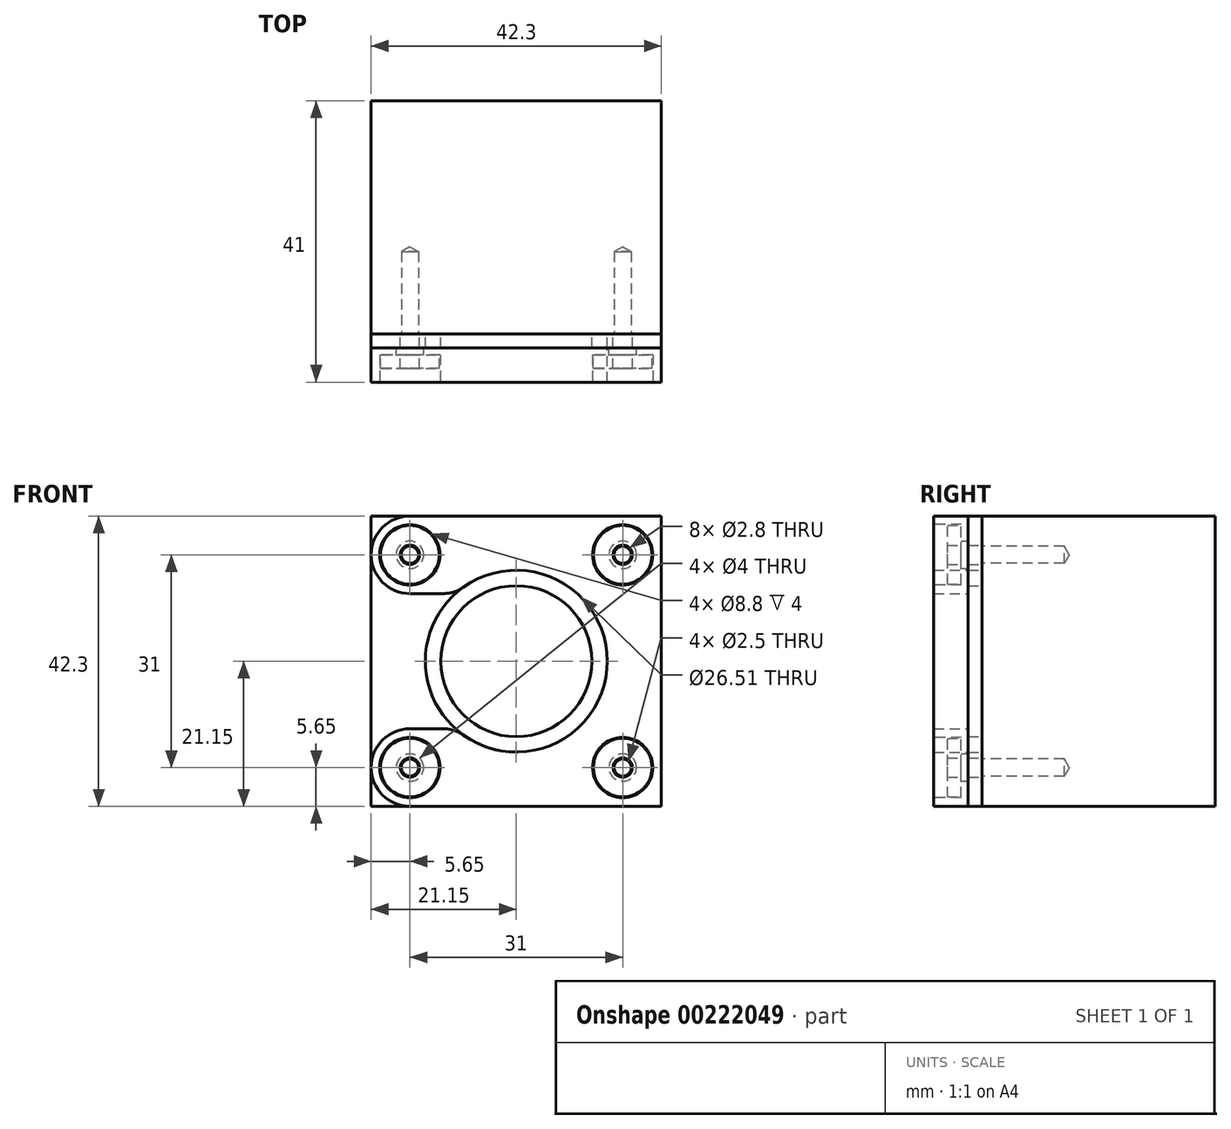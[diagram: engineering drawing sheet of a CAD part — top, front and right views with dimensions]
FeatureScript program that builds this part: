
annotation { "Feature Type Name" : "Feature", "Feature Type Description" : "" }
export const myFeature = defineFeature(function(context is Context, id is Id, definition is map)
    precondition{}
    {
        {
            var Q0;
            Q0=qCreatedBy(makeId("Front.planeOp"),FACE);
            var sketch = newSketch(context, id + "F0", { "sketchPlane" : qUnion([Q0])});
            skLineSegment(sketch, "E0.bottom", {"start": v(21.15, -21.15) * mm, "end": v(-21.15, -21.15) * mm});
            skLineSegment(sketch, "E0.top", {"start": v(21.15, 21.15) * mm, "end": v(-21.15, 21.15) * mm});
            skLineSegment(sketch, "E0.left", {"start": v(21.15, -21.15) * mm, "end": v(21.15, 21.15) * mm});
            skLineSegment(sketch, "E0.right", {"start": v(-21.15, -21.15) * mm, "end": v(-21.15, 21.15) * mm});
            skPoint(sketch, "E0.middle", {"position": v(0, 0) * mm});
            skSolve(sketch);
        }
        {
            var Q0;
            Q0=makeQuery(id+"F0.imprint","IMPRINT",FACE,{"disambiguationData":[TD([[makeQuery(id+"F0.imprint","IMPRINT",EDGE,{"derivedFrom":sQuery(id+"F0.wireOp",EDGE,"E0.bottom")}),-1.0]])]});
            extrude(context, id + "F1", {"entities" : qUnion([Q0]), "depth" : 34 * mm, "offsetDistance" : 25 * mm});
        }
        {
            var Q0;
            Q0=makeQuery(id+"F1.opExtrude","CAP_FACE",FACE,{"disambiguationData":[OSD([sQuery(id+"F0.wireOp",EDGE,"E0.bottom"),sQuery(id+"F0.wireOp",EDGE,"E0.top"),sQuery(id+"F0.wireOp",EDGE,"E0.left"),sQuery(id+"F0.wireOp",EDGE,"E0.right")])],"isStart":false});
            var sketch = newSketch(context, id + "F2", { "sketchPlane" : qUnion([Q0])});
            skCircle(sketch, "E1", {"center": v(0, 0) * mm, "radius": 11 * mm});
            skSolve(sketch);
        }
        {
            var Q0;
            Q0=makeQuery(id+"F2.imprint","IMPRINT",FACE,{"disambiguationData":[TD([[makeQuery(id+"F2.imprint","IMPRINT",EDGE,{"derivedFrom":sQuery(id+"F2.wireOp",EDGE,"E1")}),1.0]])]});
            extrude(context, id + "F3", {"entities" : qUnion([Q0]), "operationType" : NewBodyOperationType.ADD, "depth" : 2 * mm, "offsetDistance" : 25 * mm});
        }
        {
            var Q0;
            Q0=makeQuery(id+"F1.opExtrude","CAP_FACE",FACE,{"disambiguationData":[OSD([sQuery(id+"F0.wireOp",EDGE,"E0.bottom"),sQuery(id+"F0.wireOp",EDGE,"E0.top"),sQuery(id+"F0.wireOp",EDGE,"E0.left"),sQuery(id+"F0.wireOp",EDGE,"E0.right")])],"isStart":false});
            var sketch = newSketch(context, id + "F4", { "sketchPlane" : qUnion([Q0])});
            skLineSegment(sketch, "E2.bottom", {"start": v(15.5, 15.5) * mm, "end": v(-15.5, 15.5) * mm});
            skLineSegment(sketch, "E2.top", {"start": v(15.5, -15.5) * mm, "end": v(-15.5, -15.5) * mm});
            skLineSegment(sketch, "E2.left", {"start": v(15.5, 15.5) * mm, "end": v(15.5, -15.5) * mm});
            skLineSegment(sketch, "E2.right", {"start": v(-15.5, 15.5) * mm, "end": v(-15.5, -15.5) * mm});
            skPoint(sketch, "E2.middle", {"position": v(0, 0) * mm});
            skSolve(sketch);
        }
        {
            var Q0;
            Q0=sQuery(id+"F4.wireOp",VERTEX,"E2.right.start");
            var Q1;
            Q1=sQuery(id+"F4.wireOp",VERTEX,"E2.left.start");
            var Q2;
            Q2=sQuery(id+"F4.wireOp",VERTEX,"E2.left.end");
            var Q3;
            Q3=sQuery(id+"F4.wireOp",VERTEX,"E2.top.end");
            var Q4;
            Q4=makeQuery(id+"F1.opExtrude","SWEPT_BODY",BODY,{"disambiguationData":[OSD([sQuery(id+"F0.wireOp",EDGE,"E0.bottom"),sQuery(id+"F0.wireOp",EDGE,"E0.top"),sQuery(id+"F0.wireOp",EDGE,"E0.left"),sQuery(id+"F0.wireOp",EDGE,"E0.right")])]});
            hole(context, id + "F5", {"style" : HoleStyle.SIMPLE, "endStyle" : HoleEndStyle.BLIND, "holeDiameter" : 2.5 * mm, "majorDiameter" : 5 * mm, "holeDepth" : 12 * mm, "isTappedThrough" : true, "tappedDepth" : 12 * mm, "tapClearance" : 3, "locations" : qUnion([Q0, Q1, Q2, Q3]), "scope" : qUnion([Q4])});
        }
        {
            var Q0;
            Q0=makeQuery(id+"F1.opExtrude","CAP_FACE",FACE,{"disambiguationData":[OSD([sQuery(id+"F0.wireOp",EDGE,"E0.bottom"),sQuery(id+"F0.wireOp",EDGE,"E0.top"),sQuery(id+"F0.wireOp",EDGE,"E0.left"),sQuery(id+"F0.wireOp",EDGE,"E0.right")])],"isStart":false});
            var sketch = newSketch(context, id + "F6", { "sketchPlane" : qUnion([Q0])});
            skCircle(sketch, "E3.0", {"center": v(0, 0) * mm, "radius": 13.25 * mm});
            skCircle(sketch, "E4.0", {"center": v(15.5, 15.5) * mm, "radius": 1.25 * mm});
            skCircle(sketch, "E4.1", {"center": v(15.5, -15.5) * mm, "radius": 1.25 * mm});
            skCircle(sketch, "E4.2", {"center": v(-15.5, -15.5) * mm, "radius": 1.25 * mm});
            skCircle(sketch, "E4.3", {"center": v(-15.5, 15.5) * mm, "radius": 1.25 * mm});
            skCircle(sketch, "E5", {"center": v(15.5, 15.5) * mm, "radius": 1.4 * mm});
            skCircle(sketch, "E6", {"center": v(-15.5, 15.5) * mm, "radius": 1.4 * mm});
            skCircle(sketch, "E7", {"center": v(15.5, -15.5) * mm, "radius": 1.4 * mm});
            skCircle(sketch, "E8", {"center": v(-15.5, -15.5) * mm, "radius": 1.4 * mm});
            skSolve(sketch);
        }
        {
            var Q0;
            Q0=makeQuery(id+"F6.imprint","IMPRINT",FACE,{"disambiguationData":[TD([[makeQuery(id+"F6.imprint","IMPRINT",EDGE,{"derivedFrom":sQuery(id+"F6.wireOp",EDGE,"E3.0")}),-1.0]])]});
            extrude(context, id + "F7", {"entities" : qUnion([Q0]), "depth" : 2 * mm, "offsetDistance" : 25 * mm});
        }
        {
            var Q0;
            Q0=makeQuery(id+"F7.opExtrude","CAP_FACE",FACE,{"disambiguationData":[OSD([sQuery(id+"F0.wireOp",EDGE,"E0.bottom"),sQuery(id+"F0.wireOp",EDGE,"E0.top"),sQuery(id+"F0.wireOp",EDGE,"E0.left"),sQuery(id+"F0.wireOp",EDGE,"E0.right"),sQuery(id+"F6.wireOp",EDGE,"E3.0"),sQuery(id+"F6.wireOp",EDGE,"E5"),sQuery(id+"F6.wireOp",EDGE,"E6"),sQuery(id+"F6.wireOp",EDGE,"E7"),sQuery(id+"F6.wireOp",EDGE,"E8")])],"isStart":false});
            var sketch = newSketch(context, id + "F8", { "sketchPlane" : qUnion([Q0])});
            skCircle(sketch, "E9.0", {"center": v(-15.5, 15.5) * mm, "radius": 1.4 * mm});
            skCircle(sketch, "E10", {"center": v(-15.5, 15.5) * mm, "radius": 5.65 * mm});
            skCircle(sketch, "E11", {"center": v(15.5, 15.5) * mm, "radius": 5.65 * mm});
            skCircle(sketch, "E12", {"center": v(15.5, -15.5) * mm, "radius": 5.65 * mm});
            skCircle(sketch, "E13", {"center": v(-15.5, -15.5) * mm, "radius": 5.65 * mm});
            skLineSegment(sketch, "E14.0", {"start": v(15.5, 21.15) * mm, "end": v(-15.5, 21.15) * mm});
            skLineSegment(sketch, "E15.0", {"start": v(21.15, -15.5) * mm, "end": v(21.15, 15.5) * mm});
            skLineSegment(sketch, "E16.0", {"start": v(15.5, -21.15) * mm, "end": v(-15.5, -21.15) * mm});
            skLineSegment(sketch, "E17", {"start": v(-15.5, 9.85) * mm, "end": v(-8.87, 9.85) * mm});
            skLineSegment(sketch, "E18", {"start": v(-15.5, -9.85) * mm, "end": v(-8.87, -9.85) * mm});
            skPoint(sketch, "E19.orphan", {"position": v(21.15, 21.15) * mm});
            skPoint(sketch, "E20.orphan", {"position": v(-21.15, 21.15) * mm});
            skPoint(sketch, "E21.orphan", {"position": v(21.15, -21.15) * mm});
            skPoint(sketch, "E22.orphan", {"position": v(-21.15, -21.15) * mm});
            skCircle(sketch, "E23", {"center": v(15.5, 15.5) * mm, "radius": 2 * mm});
            skCircle(sketch, "E24", {"center": v(-15.5, 15.5) * mm, "radius": 2 * mm});
            skCircle(sketch, "E25", {"center": v(15.5, -15.5) * mm, "radius": 2 * mm});
            skCircle(sketch, "E26", {"center": v(-15.5, -15.5) * mm, "radius": 2 * mm});
            skSolve(sketch);
        }
        {
            var Q0;
            Q0=makeQuery(id+"F8.imprint","IMPRINT",FACE,{"disambiguationData":[TD([[makeQuery(id+"F8.imprint","IMPRINT",EDGE,{"derivedFrom":sQuery(id+"F8.wireOp",EDGE,"E23")}),-1.0]])]});
            var Q1;
            {var subQ1=makeQuery(id+"F7.opExtrude","CAP_EDGE",EDGE,{"disambiguationData":[OSD([sQuery(id+"F0.wireOp",EDGE,"E0.top")])],"isStart":false});var subQ3=makeQuery(id+"F7.opExtrude","CAP_EDGE",EDGE,{"disambiguationData":[OSD([sQuery(id+"F0.wireOp",EDGE,"E0.left")])],"isStart":false});var subQ5=makeQuery(id+"F8.imprint","INTERSECT",VERTEX,{"derivedFrom":[subQ1,subQ3]});Q1=makeQuery(id+"F8.imprint","IMPRINT",FACE,{"disambiguationData":[TD([[makeQuery(id+"F8.imprint","IMPRINT",EDGE,{"disambiguationData":[TD([[subQ5,-1.0]])],"derivedFrom":subQ1}),1.0]])]});}
            var Q2;
            {var subQ9=sQuery(id+"F8.wireOp",EDGE,"E14.0");Q2=makeQuery(id+"F8.imprint","IMPRINT",FACE,{"disambiguationData":[TD([[makeQuery(id+"F8.imprint","IMPRINT",EDGE,{"derivedFrom":subQ9}),1.0]])]});}
            var Q3;
            Q3=makeQuery(id+"F8.imprint","IMPRINT",FACE,{"disambiguationData":[TD([[makeQuery(id+"F8.imprint","IMPRINT",EDGE,{"derivedFrom":sQuery(id+"F8.wireOp",EDGE,"E25")}),-1.0]])]});
            var Q4;
            {var subQ1=makeQuery(id+"F7.opExtrude","CAP_EDGE",EDGE,{"disambiguationData":[OSD([sQuery(id+"F0.wireOp",EDGE,"E0.left")])],"isStart":false});var subQ3=makeQuery(id+"F7.opExtrude","CAP_EDGE",EDGE,{"disambiguationData":[OSD([sQuery(id+"F0.wireOp",EDGE,"E0.bottom")])],"isStart":false});var subQ5=makeQuery(id+"F8.imprint","INTERSECT",VERTEX,{"derivedFrom":[subQ3,subQ1]});Q4=makeQuery(id+"F8.imprint","IMPRINT",FACE,{"disambiguationData":[TD([[makeQuery(id+"F8.imprint","IMPRINT",EDGE,{"disambiguationData":[TD([[subQ5,-1.0]])],"derivedFrom":subQ3}),-1.0]])]});}
            var Q5;
            Q5=makeQuery(id+"F8.imprint","IMPRINT",FACE,{"disambiguationData":[TD([[makeQuery(id+"F8.imprint","IMPRINT",EDGE,{"derivedFrom":sQuery(id+"F8.wireOp",EDGE,"E24")}),-1.0]])]});
            var Q6;
            Q6=makeQuery(id+"F8.imprint","IMPRINT",FACE,{"disambiguationData":[TD([[makeQuery(id+"F8.imprint","IMPRINT",EDGE,{"derivedFrom":sQuery(id+"F8.wireOp",EDGE,"E26")}),-1.0]])]});
            var Q7;
            Q7=sQuery(id+"F8.wireOp",EDGE,"E17");
            var Q8;
            Q8=sQuery(id+"F8.wireOp",EDGE,"E18");
            extrude(context, id + "F9", {"entities" : qUnion([Q0, Q1, Q2, Q3, Q4, Q5, Q6]), "surfaceEntities" : qUnion([Q7, Q8]), "depth" : 5 * mm, "offsetDistance" : 25 * mm});
        }
        {
            var Q0;
            Q0=makeQuery(id+"F9.opExtrude","SWEPT_EDGE",EDGE,{"disambiguationData":[OSD([sQuery(id+"F6.wireOp",EDGE,"E3.0"),sQuery(id+"F8.wireOp",EDGE,"E18")])]});
            var Q1;
            Q1=makeQuery(id+"F9.opExtrude","SWEPT_EDGE",EDGE,{"disambiguationData":[OSD([sQuery(id+"F6.wireOp",EDGE,"E3.0"),sQuery(id+"F8.wireOp",EDGE,"E17")])]});
            fillet(context, id + "F10", {"entities" : qUnion([Q0, Q1]), "radius" : 5 * mm, "tangentPropagation" : true, "allowEdgeOverflow" : false});
        }
        {
            var Q0;
            Q0=makeQuery(id+"F9.opExtrude","CAP_FACE",FACE,{"disambiguationData":[OSD([sQuery(id+"F0.wireOp",EDGE,"E0.bottom"),sQuery(id+"F0.wireOp",EDGE,"E0.top"),sQuery(id+"F0.wireOp",EDGE,"E0.left"),sQuery(id+"F0.wireOp",EDGE,"E0.right"),sQuery(id+"F6.wireOp",EDGE,"E3.0"),sQuery(id+"F6.wireOp",EDGE,"E5"),sQuery(id+"F6.wireOp",EDGE,"E7"),sQuery(id+"F6.wireOp",EDGE,"E8"),sQuery(id+"F8.wireOp",EDGE,"E9.0"),sQuery(id+"F8.wireOp",EDGE,"E10"),sQuery(id+"F8.wireOp",EDGE,"E13"),sQuery(id+"F8.wireOp",EDGE,"E14.0"),sQuery(id+"F8.wireOp",EDGE,"E15.0"),sQuery(id+"F8.wireOp",EDGE,"E16.0"),sQuery(id+"F8.wireOp",EDGE,"E17"),sQuery(id+"F8.wireOp",EDGE,"E18")])],"isStart":false});
            var sketch = newSketch(context, id + "F11", { "sketchPlane" : qUnion([Q0])});
            skCircle(sketch, "E27.0", {"center": v(15.5, 15.5) * mm, "radius": 4.4 * mm});
            skCircle(sketch, "E28.0", {"center": v(15.5, -15.5) * mm, "radius": 4.4 * mm});
            skCircle(sketch, "E29.0", {"center": v(-15.5, -15.5) * mm, "radius": 4.4 * mm});
            skCircle(sketch, "E30.0", {"center": v(-15.5, 15.5) * mm, "radius": 4.4 * mm});
            skSolve(sketch);
        }
        {
            var Q0;
            Q0=makeQuery(id+"F11.imprint","IMPRINT",FACE,{"disambiguationData":[TD([[makeQuery(id+"F11.imprint","IMPRINT",EDGE,{"derivedFrom":sQuery(id+"F11.wireOp",EDGE,"E30.0")}),1.0]])]});
            var Q1;
            Q1=makeQuery(id+"F11.imprint","IMPRINT",FACE,{"disambiguationData":[TD([[makeQuery(id+"F11.imprint","IMPRINT",EDGE,{"derivedFrom":sQuery(id+"F11.wireOp",EDGE,"E27.0")}),1.0]])]});
            var Q2;
            Q2=makeQuery(id+"F11.imprint","IMPRINT",FACE,{"disambiguationData":[TD([[makeQuery(id+"F11.imprint","IMPRINT",EDGE,{"derivedFrom":sQuery(id+"F11.wireOp",EDGE,"E28.0")}),1.0]])]});
            var Q3;
            Q3=makeQuery(id+"F11.imprint","IMPRINT",FACE,{"disambiguationData":[TD([[makeQuery(id+"F11.imprint","IMPRINT",EDGE,{"derivedFrom":sQuery(id+"F11.wireOp",EDGE,"E29.0")}),1.0]])]});
            extrude(context, id + "F12", {"entities" : qUnion([Q0, Q1, Q2, Q3]), "operationType" : NewBodyOperationType.REMOVE, "oppositeDirection" : true, "depth" : 4 * mm, "offsetDistance" : 25 * mm});
        }
        {
            var Q0;
            Q0=makeQuery(id+"F12.boolean.opBoolean","COPY",FACE,{"derivedFrom":makeQuery(id+"F12.opExtrude","CAP_FACE",FACE,{"disambiguationData":[OSD([sQuery(id+"F8.wireOp",EDGE,"E23"),sQuery(id+"F11.wireOp",EDGE,"E27.0")])],"isStart":false})});
            var sketch = newSketch(context, id + "F13", { "sketchPlane" : qUnion([Q0])});
            skCircle(sketch, "E31.0", {"center": v(15.5, 15.5) * mm, "radius": 4.28 * mm});
            skCircle(sketch, "E32", {"center": v(15.5, 15.5) * mm, "radius": 1.4 * mm});
            skCircle(sketch, "E33.0", {"center": v(-15.5, 15.5) * mm, "radius": 4.28 * mm});
            skCircle(sketch, "E34", {"center": v(-15.5, 15.5) * mm, "radius": 1.4 * mm});
            skCircle(sketch, "E35.0", {"center": v(-15.5, -15.5) * mm, "radius": 4.28 * mm});
            skCircle(sketch, "E36", {"center": v(-15.5, -15.5) * mm, "radius": 1.4 * mm});
            skCircle(sketch, "E37.0", {"center": v(15.5, -15.5) * mm, "radius": 4.28 * mm});
            skCircle(sketch, "E38", {"center": v(15.5, -15.5) * mm, "radius": 1.4 * mm});
            skSolve(sketch);
        }
        {
            var Q0;
            Q0=makeQuery(id+"F13.imprint","IMPRINT",FACE,{"disambiguationData":[TD([[makeQuery(id+"F13.imprint","IMPRINT",EDGE,{"derivedFrom":sQuery(id+"F13.wireOp",EDGE,"E35.0")}),1.0]])]});
            var Q1;
            Q1=makeQuery(id+"F13.imprint","IMPRINT",FACE,{"disambiguationData":[TD([[makeQuery(id+"F13.imprint","IMPRINT",EDGE,{"derivedFrom":sQuery(id+"F13.wireOp",EDGE,"E37.0")}),1.0]])]});
            var Q2;
            Q2=makeQuery(id+"F13.imprint","IMPRINT",FACE,{"disambiguationData":[TD([[makeQuery(id+"F13.imprint","IMPRINT",EDGE,{"derivedFrom":sQuery(id+"F13.wireOp",EDGE,"E31.0")}),1.0]])]});
            var Q3;
            Q3=makeQuery(id+"F13.imprint","IMPRINT",FACE,{"disambiguationData":[TD([[makeQuery(id+"F13.imprint","IMPRINT",EDGE,{"derivedFrom":sQuery(id+"F13.wireOp",EDGE,"E33.0")}),1.0]])]});
            var Q4;
            Q4=makeQuery(id+"F13.imprint","IMPRINT",FACE,{"disambiguationData":[TD([[makeQuery(id+"F13.imprint","IMPRINT",EDGE,{"derivedFrom":sQuery(id+"F13.wireOp",EDGE,"E32")}),-1.0]])]});
            extrude(context, id + "F14", {"entities" : qUnion([Q0, Q1, Q2, Q3, Q4]), "depth" : 2 * mm, "offsetDistance" : 25 * mm});
        }
    });
